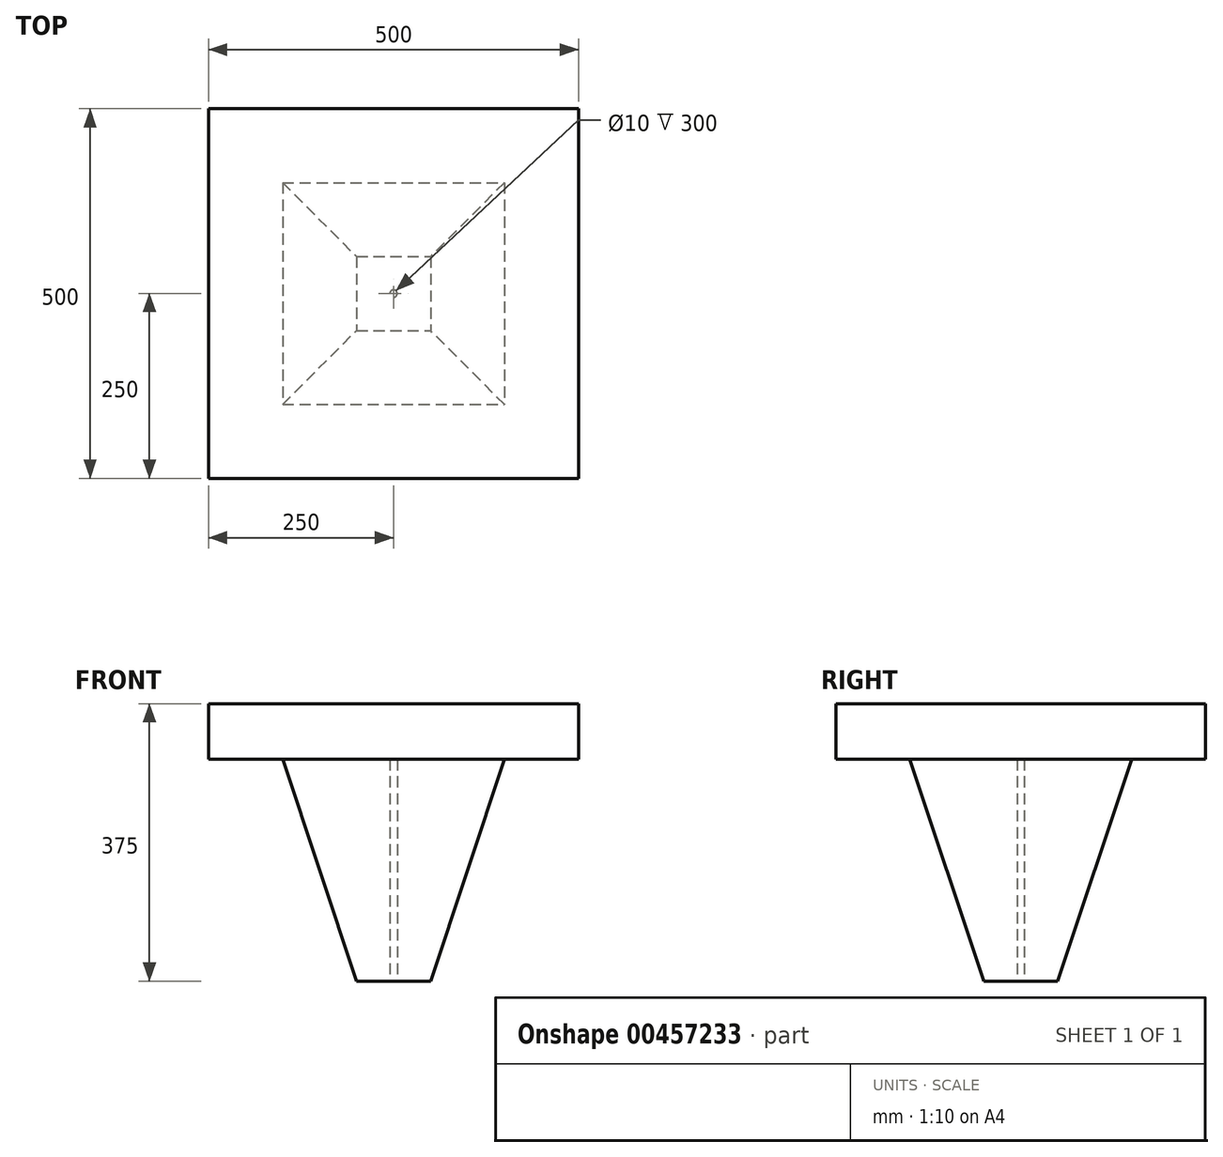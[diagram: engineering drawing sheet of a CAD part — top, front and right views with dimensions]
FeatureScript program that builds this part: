
annotation { "Feature Type Name" : "Feature", "Feature Type Description" : "" }
export const myFeature = defineFeature(function(context is Context, id is Id, definition is map)
    precondition{}
    {
        {
            var Q0;
            Q0=qCreatedBy(makeId("Top.planeOp"),FACE);
            var sketch = newSketch(context, id + "F0", { "sketchPlane" : qUnion([Q0])});
            skLineSegment(sketch, "E0.bottom", {"start": v(-250, 250) * mm, "end": v(250, 250) * mm});
            skLineSegment(sketch, "E0.top", {"start": v(-250, -250) * mm, "end": v(250, -250) * mm});
            skLineSegment(sketch, "E0.left", {"start": v(-250, 250) * mm, "end": v(-250, -250) * mm});
            skLineSegment(sketch, "E0.right", {"start": v(250, 250) * mm, "end": v(250, -250) * mm});
            skPoint(sketch, "E0.middle", {"position": v(0, 0) * mm});
            skSolve(sketch);
        }
        {
            var Q0;
            Q0=makeQuery(id+"F0.imprint","IMPRINT",FACE,{"disambiguationData":[TD([[makeQuery(id+"F0.imprint","IMPRINT",EDGE,{"derivedFrom":sQuery(id+"F0.wireOp",EDGE,"E0.bottom")}),-1.0]])]});
            extrude(context, id + "F1", {"entities" : qUnion([Q0]), "depth" : 75 * mm});
        }
        {
            var Q0;
            Q0=makeQuery(id+"F1.opExtrude","CAP_FACE",FACE,{"disambiguationData":[OSD([sQuery(id+"F0.wireOp",EDGE,"E0.bottom"),sQuery(id+"F0.wireOp",EDGE,"E0.top"),sQuery(id+"F0.wireOp",EDGE,"E0.left"),sQuery(id+"F0.wireOp",EDGE,"E0.right")])],"isStart":true});
            var sketch = newSketch(context, id + "F2", { "sketchPlane" : qUnion([Q0])});
            skLineSegment(sketch, "E1.bottom", {"start": v(-150, -150) * mm, "end": v(150, -150) * mm});
            skLineSegment(sketch, "E1.top", {"start": v(-150, 150) * mm, "end": v(150, 150) * mm});
            skLineSegment(sketch, "E1.left", {"start": v(-150, -150) * mm, "end": v(-150, 150) * mm});
            skLineSegment(sketch, "E1.right", {"start": v(150, -150) * mm, "end": v(150, 150) * mm});
            skPoint(sketch, "E1.middle", {"position": v(0, 0) * mm});
            skSolve(sketch);
        }
        {
            var Q0;
            Q0=makeQuery(id+"F2.imprint","IMPRINT",FACE,{"disambiguationData":[TD([[makeQuery(id+"F2.imprint","IMPRINT",EDGE,{"derivedFrom":sQuery(id+"F2.wireOp",EDGE,"E1.bottom")}),-1.0]])]});
            cPlane(context, id + "F3", {"entities" : qUnion([Q0]), "cplaneType" : CPlaneType.OFFSET, "offset" : 300 * mm, "width" : 150 * mm, "height" : 150 * mm});
        }
        {
            var Q0;
            Q0=qCreatedBy(id+"F3.planeOp",FACE);
            var sketch = newSketch(context, id + "F4", { "sketchPlane" : qUnion([Q0])});
            skLineSegment(sketch, "E2.bottom", {"start": v(-50, -50) * mm, "end": v(50, -50) * mm});
            skLineSegment(sketch, "E2.top", {"start": v(-50, 50) * mm, "end": v(50, 50) * mm});
            skLineSegment(sketch, "E2.left", {"start": v(-50, -50) * mm, "end": v(-50, 50) * mm});
            skLineSegment(sketch, "E2.right", {"start": v(50, -50) * mm, "end": v(50, 50) * mm});
            skPoint(sketch, "E2.middle", {"position": v(0, 0) * mm});
            skSolve(sketch);
        }
        {
            var Q1;
            Q1=makeQuery(id+"F2.imprint","IMPRINT",FACE,{"disambiguationData":[TD([[makeQuery(id+"F2.imprint","IMPRINT",EDGE,{"derivedFrom":sQuery(id+"F2.wireOp",EDGE,"E1.bottom")}),1.0]])]});
            var Q2;
            Q2=makeQuery(id+"F4.imprint","IMPRINT",FACE,{"disambiguationData":[TD([[makeQuery(id+"F4.imprint","IMPRINT",EDGE,{"derivedFrom":sQuery(id+"F4.wireOp",EDGE,"E2.bottom")}),1.0]])]});
            loft(context, id + "F5", {"operationType" : NewBodyOperationType.ADD, "sheetProfilesArray" : [{ "sheetProfileEntities" : qUnion([Q1]) }, { "sheetProfileEntities" : qUnion([Q2]) }]});
        }
        {
            var Q0;
            Q0=makeQuery(id+"F5.opLoft","CAP_FACE",FACE,{"disambiguationData":[OSD([makeQuery(id+"F4.imprint","IMPRINT",FACE,{"disambiguationData":[TD([[makeQuery(id+"F4.imprint","IMPRINT",EDGE,{"derivedFrom":sQuery(id+"F4.wireOp",EDGE,"E2.bottom")}),1.0]])]})])],"isStart":true});
            var sketch = newSketch(context, id + "F6", { "sketchPlane" : qUnion([Q0])});
            skCircle(sketch, "E3", {"center": v(0, 0) * mm, "radius": 5 * mm});
            skSolve(sketch);
        }
        {
            var Q0;
            Q0 = qSketchRegion(id + "F6", true);
            extrude(context, id + "F7", {"entities" : qUnion([Q0]), "operationType" : NewBodyOperationType.REMOVE, "oppositeDirection" : true, "depth" : 300 * mm});
        }
    });
